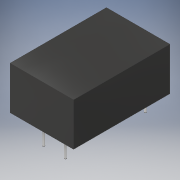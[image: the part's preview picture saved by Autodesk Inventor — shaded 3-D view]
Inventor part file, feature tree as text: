
AUTODESK INVENTOR PART (.ipt)
format: ipt  version: 2018 (Build 220112000, 112)  size: 112,640 bytes
history: native  units: in
note: dims shown in document units (in); Inventor stores cm internally (conversion verified against a paired STEP export)
features: extrude x2, sketch x2, projected_geometry x1
ambient origin geometry x8: Origin, YZ Plane, XZ Plane, XY Plane, X Axis, Y Axis, Z Axis, Center Point
bodies: Solid1 (feature_tree)
feature tree (5):
  extrude  "Extrusion1"  Depth=0.874in
  extrude  "Extrusion2"  Depth=0.2756in
  sketch  "Sketch1"  dims[d0=1.3268in d1=0.874in]
  sketch  "Sketch2"  dims[d2=0.6634in d3=0.437in d4=0.5906in d5=0.0in d6=0.0276in d7=0.0276in d8=0.0276in d9=0.0276in d10=0.2992in d11=0.5984in d12=1.1024in d14=0.1122in d15=0.2756in d16=0.0in]
  projected_geometry  "Projected Loop1"
